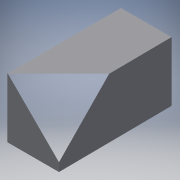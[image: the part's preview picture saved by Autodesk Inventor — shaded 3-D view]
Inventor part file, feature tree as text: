
AUTODESK INVENTOR PART (.ipt)
format: ipt  version: 2016 (Build 200138000, 138)  size: 138,240 bytes
history: native  units: mm
features: reference x5, extrude x4, sketch x4, projected_geometry x2
ambient origin geometry x8: Origin, YZ Plane, XZ Plane, XY Plane, X Axis, Y Axis, Z Axis, Center Point
bodies: Solid1 (feature_tree)
feature tree (15):
  extrude  "Extrusion1"  Depth=0.5mm
  extrude  "Extrusion2"  Depth=3.0mm
  extrude  "Extrusion3"  Depth=3.0mm TaperAngle=0.0deg
  extrude  "Extrusion4"  [1 undecoded]
  sketch  "Sketch1"  dims[d0=0.5mm d1=0.5mm]
  reference  "Reference1"
  reference  "Reference2"
  sketch  "Sketch2"  dims[d2=12.41mm d3=0.0mm d4=3.0mm]
  reference  "Reference3"
  sketch  "Sketch3"  dims[d5=12.41mm d6=0.0mm d7=3.0mm d8=0.0mm]
  reference  "Reference4"
  projected_geometry  "Projected Loop1"
  sketch  "Sketch4"  dims[d9=3.0mm d10=0.0mm]
  projected_geometry  "Projected Loop2"
  reference  "Reference5"
note: 1 required parameter value undecoded (feature->parameter linkage not recoverable at this tier; creation-order binding heuristic only, values carry confidence <= 0.55)
